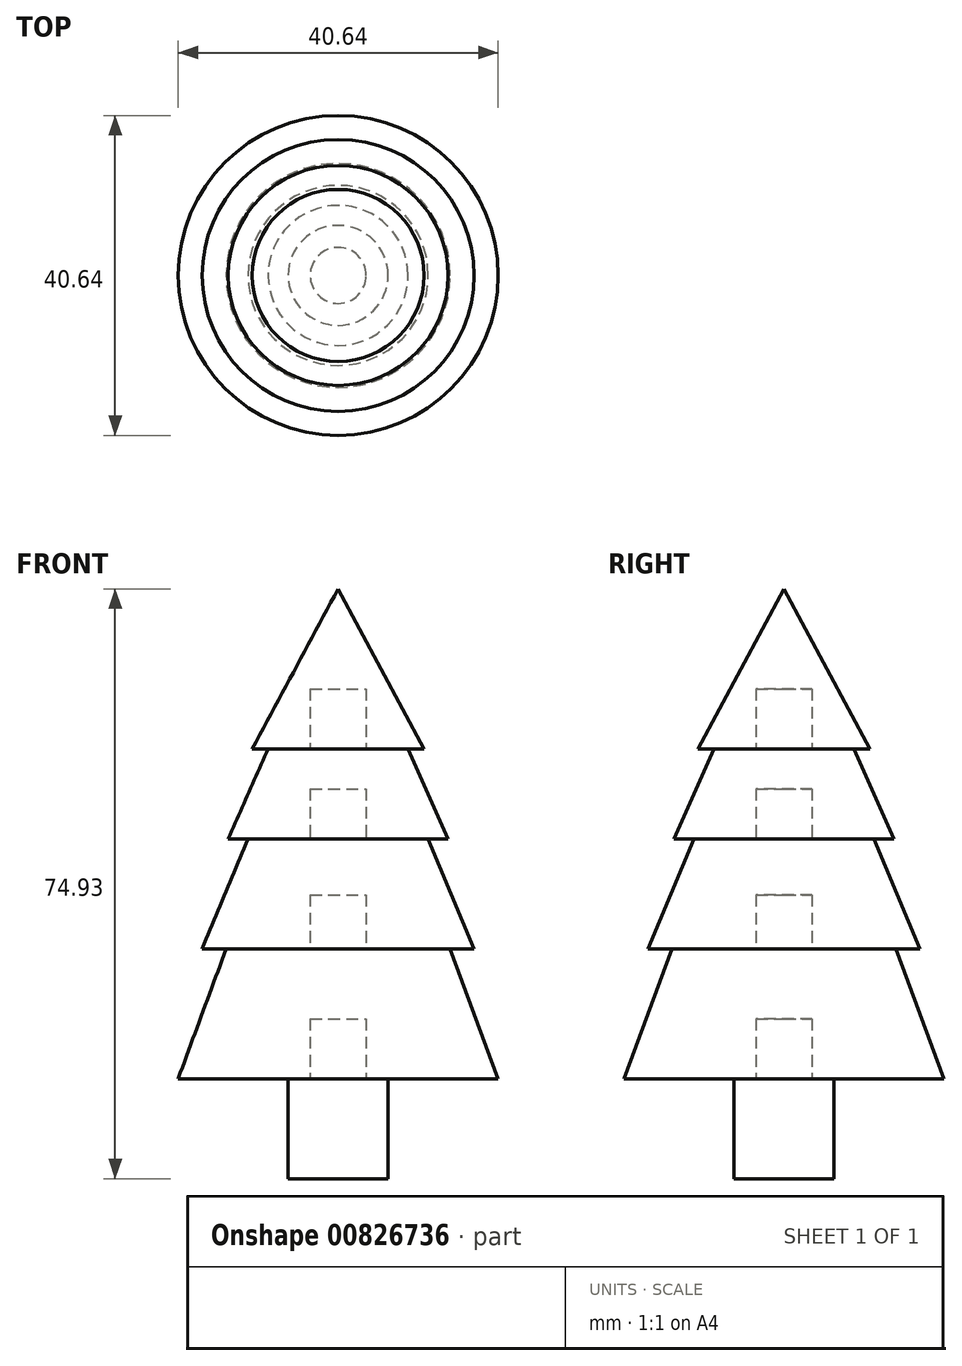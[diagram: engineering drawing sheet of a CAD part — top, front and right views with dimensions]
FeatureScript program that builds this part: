
annotation { "Feature Type Name" : "Feature", "Feature Type Description" : "" }
export const myFeature = defineFeature(function(context is Context, id is Id, definition is map)
    precondition{}
    {
        {
            var Q0;
            Q0=qCreatedBy(makeId("Top.planeOp"),FACE);
            var sketch = newSketch(context, id + "F0", { "sketchPlane" : qUnion([Q0])});
            skCircle(sketch, "E0", {"center": v(0, 0) * mm, "radius": 6.35 * mm});
            skSolve(sketch);
        }
        {
            var Q0;
            Q0=makeQuery(id+"F0.imprint","IMPRINT",FACE,{"disambiguationData":[TD([[makeQuery(id+"F0.imprint","IMPRINT",EDGE,{"derivedFrom":sQuery(id+"F0.wireOp",EDGE,"E0")}),1.0]])]});
            extrude(context, id + "F1", {"entities" : qUnion([Q0]), "depth" : 12.7 * mm, "offsetDistance" : 25.4 * mm});
        }
        {
            var Q0;
            Q0=makeQuery(id+"F1.opExtrude","CAP_FACE",FACE,{"disambiguationData":[OSD([sQuery(id+"F0.wireOp",EDGE,"E0")])],"isStart":false});
            var sketch = newSketch(context, id + "F2", { "sketchPlane" : qUnion([Q0])});
            skCircle(sketch, "E1", {"center": v(0, 0) * mm, "radius": 3.18 * mm});
            skSolve(sketch);
        }
        {
            var Q0;
            Q0=qSketchRegion(id+"F2",true);
            extrude(context, id + "F3", {"entities" : qUnion([Q0]), "operationType" : NewBodyOperationType.ADD, "depth" : 6.35 * mm});
        }
        {
            var Q0;
            Q0=qCreatedBy(makeId("Front.planeOp"),FACE);
            var sketch = newSketch(context, id + "F4", { "sketchPlane" : qUnion([Q0])});
            skLineSegment(sketch, "E2", {"start": v(0, 12.7) * mm, "end": v(0, 29.21) * mm});
            skLineSegment(sketch, "E3", {"start": v(0, 29.21) * mm, "end": v(14.22, 29.21) * mm});
            skLineSegment(sketch, "E4", {"start": v(14.22, 29.21) * mm, "end": v(20.32, 12.7) * mm});
            skLineSegment(sketch, "E5", {"start": v(20.32, 12.7) * mm, "end": v(0, 12.7) * mm});
            skSolve(sketch);
        }
        {
            var Q0;
            Q0=qSketchRegion(id+"F4",true);
            var Q1;
            Q1=sQuery(id+"F4.wireOp",EDGE,"E2");
            revolve(context, id + "F5", {"entities" : qUnion([Q0]), "axis" : qUnion([Q1]), "revolveType" : RevolveType.FULL});
        }
        {
            var Q0;
            Q0=makeQuery(id+"F5.opRevolve","SWEPT_FACE",FACE,{"disambiguationData":[OSD([sQuery(id+"F4.wireOp",EDGE,"E5")])]});
            var sketch = newSketch(context, id + "F6", { "sketchPlane" : qUnion([Q0])});
            skCircle(sketch, "E6", {"center": v(0, 0) * mm, "radius": 3.56 * mm});
            skSolve(sketch);
        }
        {
            var Q0;
            Q0=qSketchRegion(id+"F6",true);
            var Q1;
            Q1=sQuery(id+"F6.wireOp",EDGE,"E6");
            extrude(context, id + "F7", {"entities" : qUnion([Q0]), "operationType" : NewBodyOperationType.REMOVE, "surfaceEntities" : qUnion([Q1]), "oppositeDirection" : true, "depth" : 7.62 * mm});
        }
        {
            var Q0;
            Q0=makeQuery(id+"F5.opRevolve","SWEPT_FACE",FACE,{"disambiguationData":[OSD([sQuery(id+"F4.wireOp",EDGE,"E3")])]});
            var sketch = newSketch(context, id + "F8", { "sketchPlane" : qUnion([Q0])});
            skCircle(sketch, "E7", {"center": v(0, 0) * mm, "radius": 3.18 * mm});
            skSolve(sketch);
        }
        {
            var Q0;
            Q0=qSketchRegion(id+"F8",true);
            extrude(context, id + "F9", {"entities" : qUnion([Q0]), "operationType" : NewBodyOperationType.ADD, "depth" : 6.35 * mm});
        }
        {
            var Q0;
            Q0=qCreatedBy(makeId("Right.planeOp"),FACE);
            var sketch = newSketch(context, id + "F10", { "sketchPlane" : qUnion([Q0])});
            skLineSegment(sketch, "E8", {"start": v(0, 43.18) * mm, "end": v(-11.43, 43.18) * mm});
            skLineSegment(sketch, "E9", {"start": v(-11.43, 43.18) * mm, "end": v(-17.27, 29.21) * mm});
            skLineSegment(sketch, "E10", {"start": v(-17.27, 29.21) * mm, "end": v(0, 29.21) * mm});
            skLineSegment(sketch, "E11", {"start": v(0, 29.21) * mm, "end": v(0, 43.18) * mm});
            skSolve(sketch);
        }
        {
            var Q0;
            Q0=makeQuery(id+"F10.imprint","IMPRINT",FACE,{"disambiguationData":[TD([[makeQuery(id+"F10.imprint","IMPRINT",EDGE,{"derivedFrom":sQuery(id+"F10.wireOp",EDGE,"E8")}),1.0]])]});
            var Q1;
            Q1=qConstructionFilter(qBodyType(qCreatedBy(id+"F10",EDGE),BodyType.WIRE),ConstructionObject.NO);
            var Q2;
            Q2=sQuery(id+"F10.wireOp",EDGE,"E11");
            revolve(context, id + "F11", {"entities" : qUnion([Q0]), "surfaceEntities" : qUnion([Q1]), "axis" : qUnion([Q2]), "revolveType" : RevolveType.FULL});
        }
        {
            var Q0;
            Q0=makeQuery(id+"F11.opRevolve","SWEPT_FACE",FACE,{"disambiguationData":[OSD([sQuery(id+"F10.wireOp",EDGE,"E10")])]});
            var sketch = newSketch(context, id + "F12", { "sketchPlane" : qUnion([Q0])});
            skCircle(sketch, "E12", {"center": v(0, 0) * mm, "radius": 3.56 * mm});
            skSolve(sketch);
        }
        {
            var Q0;
            Q0=makeQuery(id+"F12.imprint","IMPRINT",FACE,{"disambiguationData":[TD([[makeQuery(id+"F12.imprint","IMPRINT",EDGE,{"derivedFrom":sQuery(id+"F12.wireOp",EDGE,"E12")}),1.0]])]});
            var Q1;
            Q1=sQuery(id+"F12.wireOp",EDGE,"E12");
            extrude(context, id + "F13", {"entities" : qUnion([Q0]), "operationType" : NewBodyOperationType.REMOVE, "surfaceEntities" : qUnion([Q1]), "oppositeDirection" : true, "depth" : 6.86 * mm});
        }
        {
            var Q0;
            Q0=makeQuery(id+"F11.opRevolve","SWEPT_FACE",FACE,{"disambiguationData":[OSD([sQuery(id+"F10.wireOp",EDGE,"E8")])]});
            var sketch = newSketch(context, id + "F14", { "sketchPlane" : qUnion([Q0])});
            skCircle(sketch, "E13", {"center": v(0, 0) * mm, "radius": 3.18 * mm});
            skSolve(sketch);
        }
        {
            var Q0;
            Q0=qSketchRegion(id+"F14",true);
            extrude(context, id + "F15", {"entities" : qUnion([Q0]), "operationType" : NewBodyOperationType.ADD, "depth" : 5.08 * mm});
        }
        {
            var Q0;
            Q0=qCreatedBy(makeId("Front.planeOp"),FACE);
            var sketch = newSketch(context, id + "F16", { "sketchPlane" : qUnion([Q0])});
            skLineSegment(sketch, "E14", {"start": v(0, 54.61) * mm, "end": v(8.9, 54.61) * mm});
            skLineSegment(sketch, "E15", {"start": v(8.9, 54.61) * mm, "end": v(13.97, 43.18) * mm});
            skLineSegment(sketch, "E16", {"start": v(13.97, 43.18) * mm, "end": v(0, 43.18) * mm});
            skLineSegment(sketch, "E17", {"start": v(0, 43.18) * mm, "end": v(0, 54.61) * mm});
            skSolve(sketch);
        }
        {
            var Q0;
            Q0=qSketchRegion(id+"F16",true);
            var Q1;
            Q1=sQuery(id+"F16.wireOp",EDGE,"E17");
            revolve(context, id + "F17", {"entities" : qUnion([Q0]), "axis" : qUnion([Q1]), "revolveType" : RevolveType.FULL});
        }
        {
            var Q0;
            Q0=makeQuery(id+"F17.opRevolve","SWEPT_FACE",FACE,{"disambiguationData":[OSD([sQuery(id+"F16.wireOp",EDGE,"E16")])]});
            var sketch = newSketch(context, id + "F18", { "sketchPlane" : qUnion([Q0])});
            skCircle(sketch, "E18", {"center": v(0, 0) * mm, "radius": 3.56 * mm});
            skSolve(sketch);
        }
        {
            var Q0;
            Q0=qSketchRegion(id+"F18",true);
            extrude(context, id + "F19", {"entities" : qUnion([Q0]), "operationType" : NewBodyOperationType.REMOVE, "oppositeDirection" : true, "depth" : 6.35 * mm});
        }
        {
            var Q0;
            Q0=makeQuery(id+"F17.opRevolve","SWEPT_FACE",FACE,{"disambiguationData":[OSD([sQuery(id+"F16.wireOp",EDGE,"E14")])]});
            var sketch = newSketch(context, id + "F20", { "sketchPlane" : qUnion([Q0])});
            skCircle(sketch, "E19", {"center": v(0, 0) * mm, "radius": 3.18 * mm});
            skSolve(sketch);
        }
        {
            var Q0;
            Q0=qSketchRegion(id+"F20",true);
            extrude(context, id + "F21", {"entities" : qUnion([Q0]), "operationType" : NewBodyOperationType.ADD, "depth" : 3.8 * mm});
        }
        {
            var Q0;
            Q0=qCreatedBy(makeId("Front.planeOp"),FACE);
            var sketch = newSketch(context, id + "F22", { "sketchPlane" : qUnion([Q0])});
            skLineSegment(sketch, "E20", {"start": v(0, 74.93) * mm, "end": v(10.92, 54.61) * mm});
            skLineSegment(sketch, "E21", {"start": v(10.92, 54.61) * mm, "end": v(0, 54.61) * mm});
            skLineSegment(sketch, "E22", {"start": v(0, 54.61) * mm, "end": v(0, 74.93) * mm});
            skSolve(sketch);
        }
        {
            var Q0;
            Q0=qSketchRegion(id+"F22",true);
            var Q1;
            Q1=sQuery(id+"F22.wireOp",EDGE,"E22");
            revolve(context, id + "F23", {"entities" : qUnion([Q0]), "axis" : qUnion([Q1]), "revolveType" : RevolveType.FULL});
        }
        {
            var Q0;
            Q0=makeQuery(id+"F23.opRevolve","SWEPT_FACE",FACE,{"disambiguationData":[OSD([sQuery(id+"F22.wireOp",EDGE,"E21")])]});
            var sketch = newSketch(context, id + "F24", { "sketchPlane" : qUnion([Q0])});
            skCircle(sketch, "E23", {"center": v(0, 0) * mm, "radius": 3.56 * mm});
            skSolve(sketch);
        }
        {
            var Q0;
            Q0=makeQuery(id+"F24.imprint","IMPRINT",FACE,{"disambiguationData":[TD([[makeQuery(id+"F24.imprint","IMPRINT",EDGE,{"derivedFrom":sQuery(id+"F24.wireOp",EDGE,"E23")}),1.0]])]});
            extrude(context, id + "F25", {"entities" : qUnion([Q0]), "operationType" : NewBodyOperationType.REMOVE, "oppositeDirection" : true, "depth" : 7.62 * mm});
        }
    });
